# Revit family: FU_Table_Sandler_TOFFEE 1-0
name_source: partatom
category: Furniture
units: mm (PartAtom-declared; Revit-internal decimal feet)

## family parameters
Always vertical = No
Cut with Voids When Loaded = No
OmniClass Number = 23.21.23.15.17
Render Appearance Source = Family Geometry
Room Calculation Point = No
Shared = No
Work Plane-Based = Yes

## types (1)
- TOFFEE 1.0
    BIMobject category = Table
    BIMobject category code = furniture-table
    BIMobject main category = Furniture
    BIMobject main category code = furniture
    Brand url = https://www.sandlerseating.com
    Default Elevation = 0 mm  [stored 0 ft]
    Depth = 750 mm  [stored 2.46063 ft]
    Description = Solid beech square coffee table with detailing at the top of legs.
    Edition number = 1
    Height = 380 mm
    IFC Classification = Furnishing Element
    Manufacturer = Sandler
    Manufacturer country = USA
    Manufacturer name = Sandler
    Masterformat 2014 Code = 12 48 43.13
    Masterformat 2014 Description = Table Mats
    Model = TOFFEE 1.0
    OmniClass Code = 23-21 23 15 17
    Product Guid = ??
    Product SKU = ??
    Product data url = https://www.sandlerseating.com
    Product family = Furniture
    Product group = Table
    Product name = TOFFEE
    Product url = https://www.sandlerseating.com
    QR code = https://www.sandlerseating.com
    URL = https://www.sandlerseating.com
    Uniformat II Description = Movable Furnishings
    Width = 750 mm  [stored 2.46063 ft]

note: [stored X ft] marks values corroborated as IEEE doubles in the binary element streams (Revit-internal decimal feet)

## geometry (parser evidence)
native form markers: Sweep x2
no freeform markers — native parametric forms only
